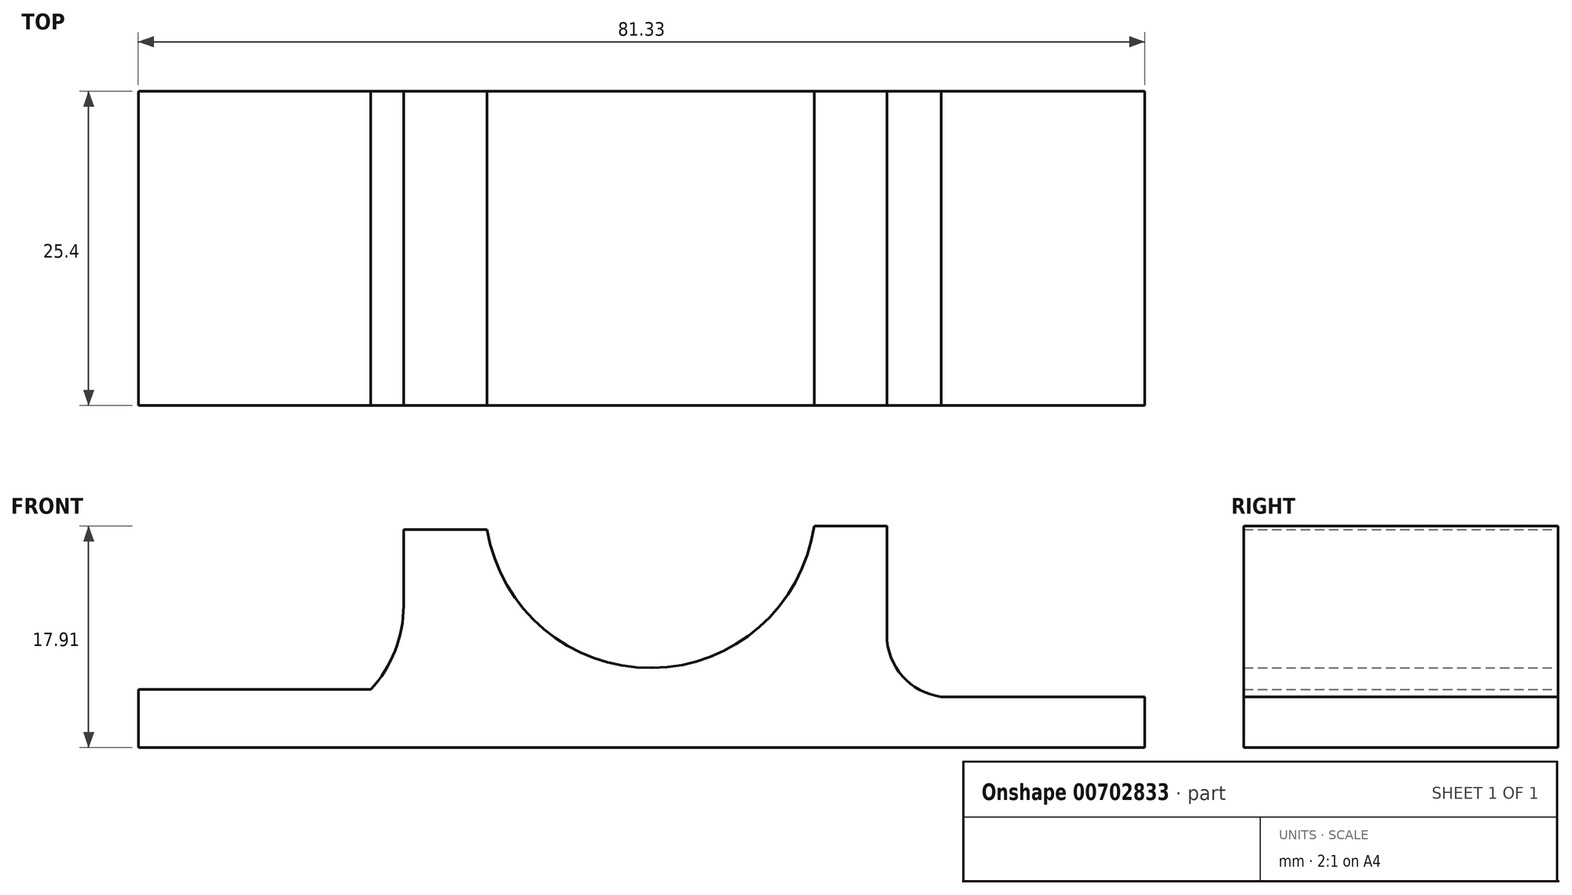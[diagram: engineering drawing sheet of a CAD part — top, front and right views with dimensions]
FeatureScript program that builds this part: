
annotation { "Feature Type Name" : "Feature", "Feature Type Description" : "" }
export const myFeature = defineFeature(function(context is Context, id is Id, definition is map)
    precondition{}
    {
        {
            var Q0;
            Q0=qCreatedBy(makeId("Front.planeOp"),FACE);
            var sketch = newSketch(context, id + "F0", { "sketchPlane" : qUnion([Q0])});
            skLineSegment(sketch, "E0", {"start": v(-40.08, -39.64) * mm, "end": v(41.25, -39.64) * mm});
            skLineSegment(sketch, "E1", {"start": v(41.25, -39.64) * mm, "end": v(41.25, -35.53) * mm});
            skLineSegment(sketch, "E2", {"start": v(41.25, -35.53) * mm, "end": v(24.81, -35.53) * mm});
            skLineSegment(sketch, "E3", {"start": v(20.4, -30.54) * mm, "end": v(20.4, -21.73) * mm});
            skLineSegment(sketch, "E4", {"start": v(20.4, -21.73) * mm, "end": v(14.53, -21.73) * mm});
            skArc(sketch, "E5", {"start": v(20.4, -30.54) * mm, "mid": v(21.66, -33.86) * mm, "end": v(24.81, -35.53) * mm});
            skLineSegment(sketch, "E6", {"start": v(-40.08, -39.64) * mm, "end": v(-40.08, -34.94) * mm});
            skLineSegment(sketch, "E7", {"start": v(-40.08, -34.94) * mm, "end": v(-21.29, -34.94) * mm});
            skLineSegment(sketch, "E8", {"start": v(-18.64, -28.19) * mm, "end": v(-18.64, -22.02) * mm});
            skLineSegment(sketch, "E9", {"start": v(-18.64, -22.02) * mm, "end": v(-11.9, -22.02) * mm});
            skArc(sketch, "E10", {"start": v(-21.29, -34.94) * mm, "mid": v(-19.33, -31.81) * mm, "end": v(-18.64, -28.19) * mm});
            skArc(sketch, "E11", {"start": v(-11.9, -22.02) * mm, "mid": v(1.45, -33.2) * mm, "end": v(14.53, -21.73) * mm});
            skSolve(sketch);
        }
        {
            var Q0;
            Q0 = qSketchRegion(id + "F0", true);
            extrude(context, id + "F1", {"entities" : qUnion([Q0]), "depth" : 25.4 * mm, "offsetDistance" : 25.4 * mm});
        }
    });
